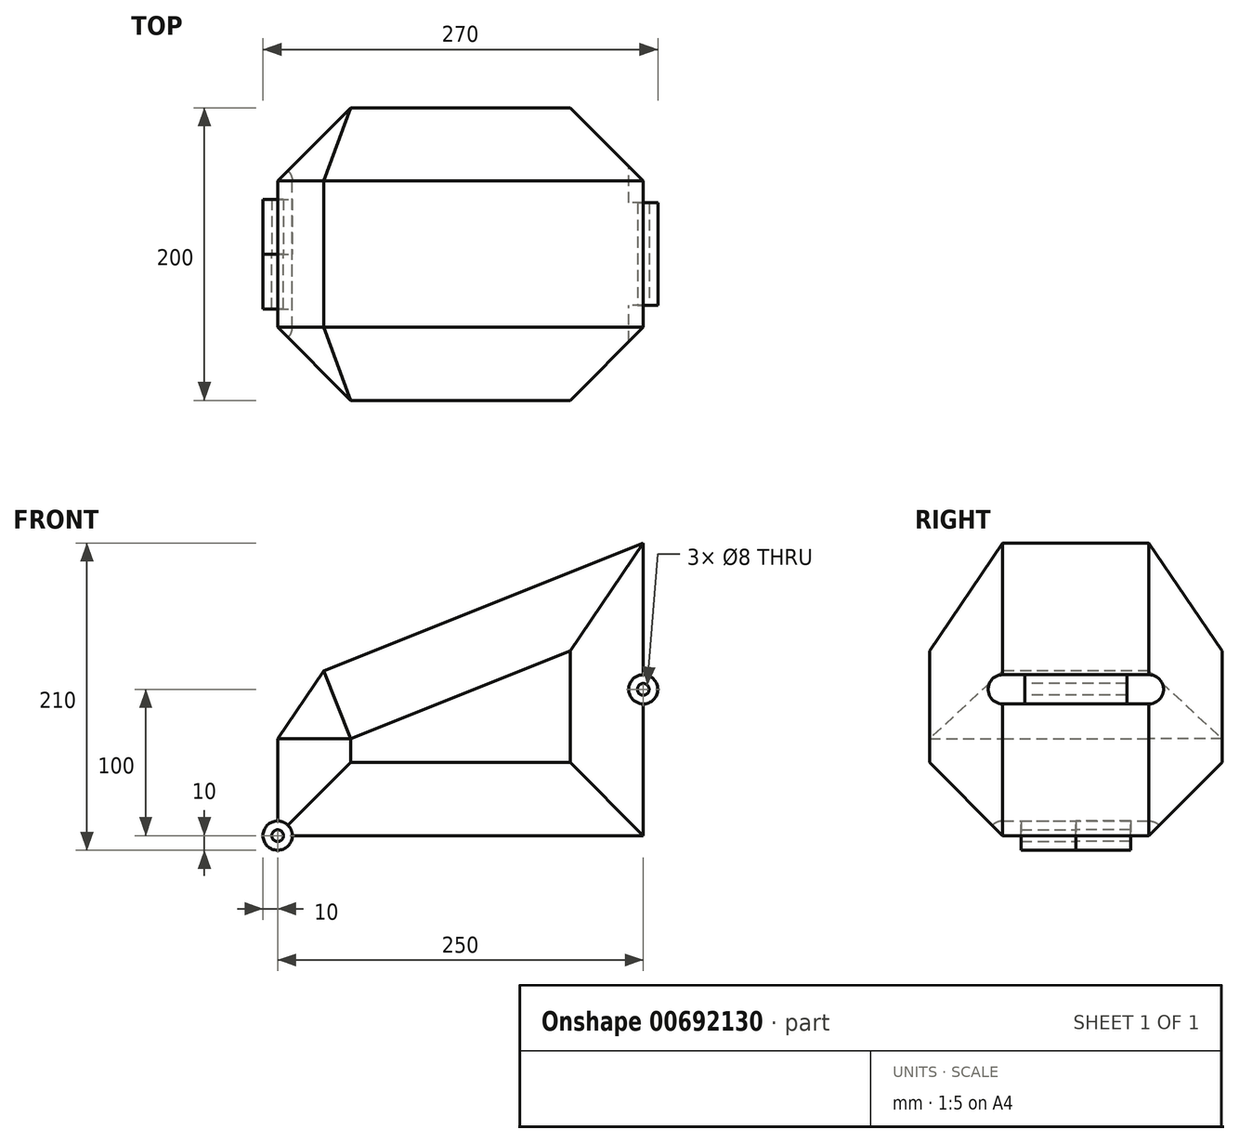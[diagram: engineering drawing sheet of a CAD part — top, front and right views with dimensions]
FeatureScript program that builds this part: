
annotation { "Feature Type Name" : "Feature", "Feature Type Description" : "" }
export const myFeature = defineFeature(function(context is Context, id is Id, definition is map)
    precondition{}
    {
        {
            var Q0;
            Q0=qCreatedBy(makeId("Front.planeOp"),FACE);
            var sketch = newSketch(context, id + "F0", { "sketchPlane" : qUnion([Q0])});
            skLineSegment(sketch, "E0.bottom", {"start": v(125, -100) * mm, "end": v(-125, -100) * mm});
            skLineSegment(sketch, "E0.left", {"start": v(125, -100) * mm, "end": v(125, 100) * mm});
            skLineSegment(sketch, "E0.right", {"start": v(-125, -100) * mm, "end": v(-125, 0) * mm});
            skPoint(sketch, "E0.middle", {"position": v(0, 0) * mm});
            skCircle(sketch, "E1", {"center": v(125, 0) * mm, "radius": 10 * mm});
            skCircle(sketch, "E2", {"center": v(125, 0) * mm, "radius": 4 * mm});
            skCircle(sketch, "E3", {"center": v(-125, -100) * mm, "radius": 10 * mm});
            skCircle(sketch, "E4", {"center": v(-125, -100) * mm, "radius": 4 * mm});
            skLineSegment(sketch, "E5", {"start": v(-125, 0) * mm, "end": v(125, 100) * mm});
            skPoint(sketch, "E0.top.end.orphan", {"position": v(-125, 100) * mm});
            skSolve(sketch);
        }
        {
            var Q0;
            {var subQ0=sQuery(id+"F0.wireOp",EDGE,"E5");Q0=makeQuery(id+"F0.imprint","IMPRINT",FACE,{"disambiguationData":[TD([[makeQuery(id+"F0.imprint","IMPRINT",EDGE,{"derivedFrom":subQ0}),-1.0]])]});}
            extrude(context, id + "F1", {"entities" : qUnion([Q0]), "depth" : 100 * mm, "offsetDistance" : 25 * mm});
        }
        {
            var Q0;
            Q0=makeQuery(id+"F1.opExtrude","CAP_FACE",FACE,{"disambiguationData":[OSD([sQuery(id+"F0.wireOp",EDGE,"E0.bottom"),sQuery(id+"F0.wireOp",EDGE,"E0.left"),sQuery(id+"F0.wireOp",EDGE,"E0.right"),sQuery(id+"F0.wireOp",EDGE,"E1"),sQuery(id+"F0.wireOp",EDGE,"E3"),sQuery(id+"F0.wireOp",EDGE,"E5")])],"isStart":true});
            extrude(context, id + "F2", {"entities" : qUnion([Q0]), "operationType" : NewBodyOperationType.ADD, "depth" : 100 * mm, "offsetDistance" : 25 * mm});
        }
        {
            var Q0;
            {var subQ0=sQuery(id+"F0.wireOp",EDGE,"E3");var subQ1=sQuery(id+"F0.wireOp",EDGE,"E0.bottom");var subQ2=makeQuery(id+"F0.imprint","INTERSECT",VERTEX,{"derivedFrom":[subQ1,subQ0]});Q0=makeQuery(id+"F0.imprint","IMPRINT",FACE,{"disambiguationData":[TD([[makeQuery(id+"F0.imprint","IMPRINT",EDGE,{"disambiguationData":[TD([[subQ2,-1.0]])],"derivedFrom":subQ1}),-1.0]])]});}
            var Q1;
            {var subQ0=sQuery(id+"F0.wireOp",EDGE,"E3");var subQ1=sQuery(id+"F0.wireOp",EDGE,"E0.bottom");var subQ2=makeQuery(id+"F0.imprint","INTERSECT",VERTEX,{"derivedFrom":[subQ1,subQ0]});Q1=makeQuery(id+"F0.imprint","IMPRINT",FACE,{"disambiguationData":[TD([[makeQuery(id+"F0.imprint","IMPRINT",EDGE,{"disambiguationData":[TD([[subQ2,-1.0]])],"derivedFrom":subQ1}),1.0]])]});}
            extrude(context, id + "F3", {"entities" : qUnion([Q0, Q1]), "depth" : 37.5 * mm, "offsetDistance" : 25 * mm});
        }
        {
            var Q0;
            {var subQ0=sQuery(id+"F0.wireOp",EDGE,"E1");var subQ1=sQuery(id+"F0.wireOp",EDGE,"E0.left");var subQ2=makeQuery(id+"F0.imprint","INTERSECT",VERTEX,{"disambiguationData":[OD(0.0)],"derivedFrom":[subQ1,subQ0]});Q0=makeQuery(id+"F0.imprint","IMPRINT",FACE,{"disambiguationData":[TD([[makeQuery(id+"F0.imprint","IMPRINT",EDGE,{"disambiguationData":[TD([[subQ2,-1.0]])],"derivedFrom":subQ1}),-1.0]])]});}
            var Q1;
            {var subQ0=sQuery(id+"F0.wireOp",EDGE,"E1");var subQ1=sQuery(id+"F0.wireOp",EDGE,"E0.left");var subQ2=makeQuery(id+"F0.imprint","INTERSECT",VERTEX,{"disambiguationData":[OD(0.0)],"derivedFrom":[subQ1,subQ0]});Q1=makeQuery(id+"F0.imprint","IMPRINT",FACE,{"disambiguationData":[TD([[makeQuery(id+"F0.imprint","IMPRINT",EDGE,{"disambiguationData":[TD([[subQ2,-1.0]])],"derivedFrom":subQ1}),1.0]])]});}
            var Q2;
            Q2=sQuery(id+"F0.wireOp",EDGE,"E2");
            var Q3;
            Q3=sQuery(id+"F0.wireOp",EDGE,"E1");
            extrude(context, id + "F4", {"entities" : qUnion([Q0, Q1]), "surfaceOperationType" : NewSurfaceOperationType.ADD, "surfaceEntities" : qUnion([Q2, Q3]), "oppositeDirection" : true, "depth" : 35 * mm, "offsetDistance" : 25 * mm});
        }
        {
            var Q0;
            Q0=makeQuery(id+"F4.opExtrude","CAP_FACE",FACE,{"disambiguationData":[OSD([sQuery(id+"F0.wireOp",EDGE,"E1"),sQuery(id+"F0.wireOp",EDGE,"E2")])],"isStart":true});
            extrude(context, id + "F5", {"entities" : qUnion([Q0]), "operationType" : NewBodyOperationType.ADD, "depth" : 35 * mm, "offsetDistance" : 25 * mm});
        }
        {
            var Q0;
            Q0=makeQuery(id+"F3.opExtrude","CAP_FACE",FACE,{"disambiguationData":[OSD([sQuery(id+"F0.wireOp",EDGE,"E3"),sQuery(id+"F0.wireOp",EDGE,"E4")])],"isStart":true});
            extrude(context, id + "F6", {"entities" : qUnion([Q0]), "depth" : 37.5 * mm, "offsetDistance" : 25 * mm});
        }
        {
            var Q0;
            Q0=makeQuery(id+"F1.opExtrude","CAP_EDGE",EDGE,{"disambiguationData":[OSD([sQuery(id+"F0.wireOp",EDGE,"E5")])],"isStart":false});
            var Q1;
            Q1=makeQuery(id+"F2.opExtrude","CAP_EDGE",EDGE,{"disambiguationData":[OSD([sQuery(id+"F0.wireOp",EDGE,"E5")])],"isStart":false});
            var Q2;
            {var subQ0=sQuery(id+"F0.wireOp",EDGE,"E5");var subQ1=sQuery(id+"F0.wireOp",EDGE,"E0.right");Q2=makeQuery(id+"F2.boolean.opBoolean","MERGE",EDGE,{"derivedFrom":[makeQuery(id+"F1.opExtrude","SWEPT_EDGE",EDGE,{"disambiguationData":[OSD([subQ1,subQ0])]}),makeQuery(id+"F2.opExtrude","SWEPT_EDGE",EDGE,{"disambiguationData":[OSD([subQ1,subQ0])]})]});}
            var Q3;
            {var subQ0=sQuery(id+"F0.wireOp",EDGE,"E0.left");Q3=makeQuery(id+"F1.opExtrude","CAP_EDGE",EDGE,{"disambiguationData":[OSD([subQ0]),TDD([makeQuery(id+"F0.imprint","IMPRINT",EDGE,{"disambiguationData":[TD([[makeQuery(id+"F0.imprint","INTERSECT",VERTEX,{"derivedFrom":[sQuery(id+"F0.wireOp",EDGE,"E0.bottom"),subQ0]}),-1.0]])],"derivedFrom":subQ0})])],"isStart":false});}
            var Q4;
            Q4=makeQuery(id+"F1.opExtrude","CAP_EDGE",EDGE,{"disambiguationData":[OSD([sQuery(id+"F0.wireOp",EDGE,"E0.right")])],"isStart":false});
            var Q5;
            Q5=makeQuery(id+"F2.opExtrude","CAP_EDGE",EDGE,{"disambiguationData":[OSD([sQuery(id+"F0.wireOp",EDGE,"E0.right")])],"isStart":false});
            var Q6;
            {var subQ0=sQuery(id+"F0.wireOp",EDGE,"E0.left");Q6=makeQuery(id+"F2.opExtrude","CAP_EDGE",EDGE,{"disambiguationData":[OSD([subQ0]),TDD([makeQuery(id+"F1.opExtrude","CAP_EDGE",EDGE,{"disambiguationData":[OSD([subQ0]),TDD([makeQuery(id+"F0.imprint","IMPRINT",EDGE,{"disambiguationData":[TD([[makeQuery(id+"F0.imprint","INTERSECT",VERTEX,{"derivedFrom":[sQuery(id+"F0.wireOp",EDGE,"E0.bottom"),subQ0]}),-1.0]])],"derivedFrom":subQ0})])],"isStart":true})])],"isStart":false});}
            var Q7;
            Q7=makeQuery(id+"F1.opExtrude","CAP_EDGE",EDGE,{"disambiguationData":[OSD([sQuery(id+"F0.wireOp",EDGE,"E0.bottom")])],"isStart":false});
            var Q8;
            Q8=makeQuery(id+"F2.opExtrude","CAP_EDGE",EDGE,{"disambiguationData":[OSD([sQuery(id+"F0.wireOp",EDGE,"E0.bottom")])],"isStart":false});
            chamfer(context, id + "F7", {"entities" : qUnion([Q0, Q1, Q2, Q3, Q4, Q5, Q6, Q7, Q8]), "width" : 50 * mm, "tangentPropagation" : true});
        }
    });
